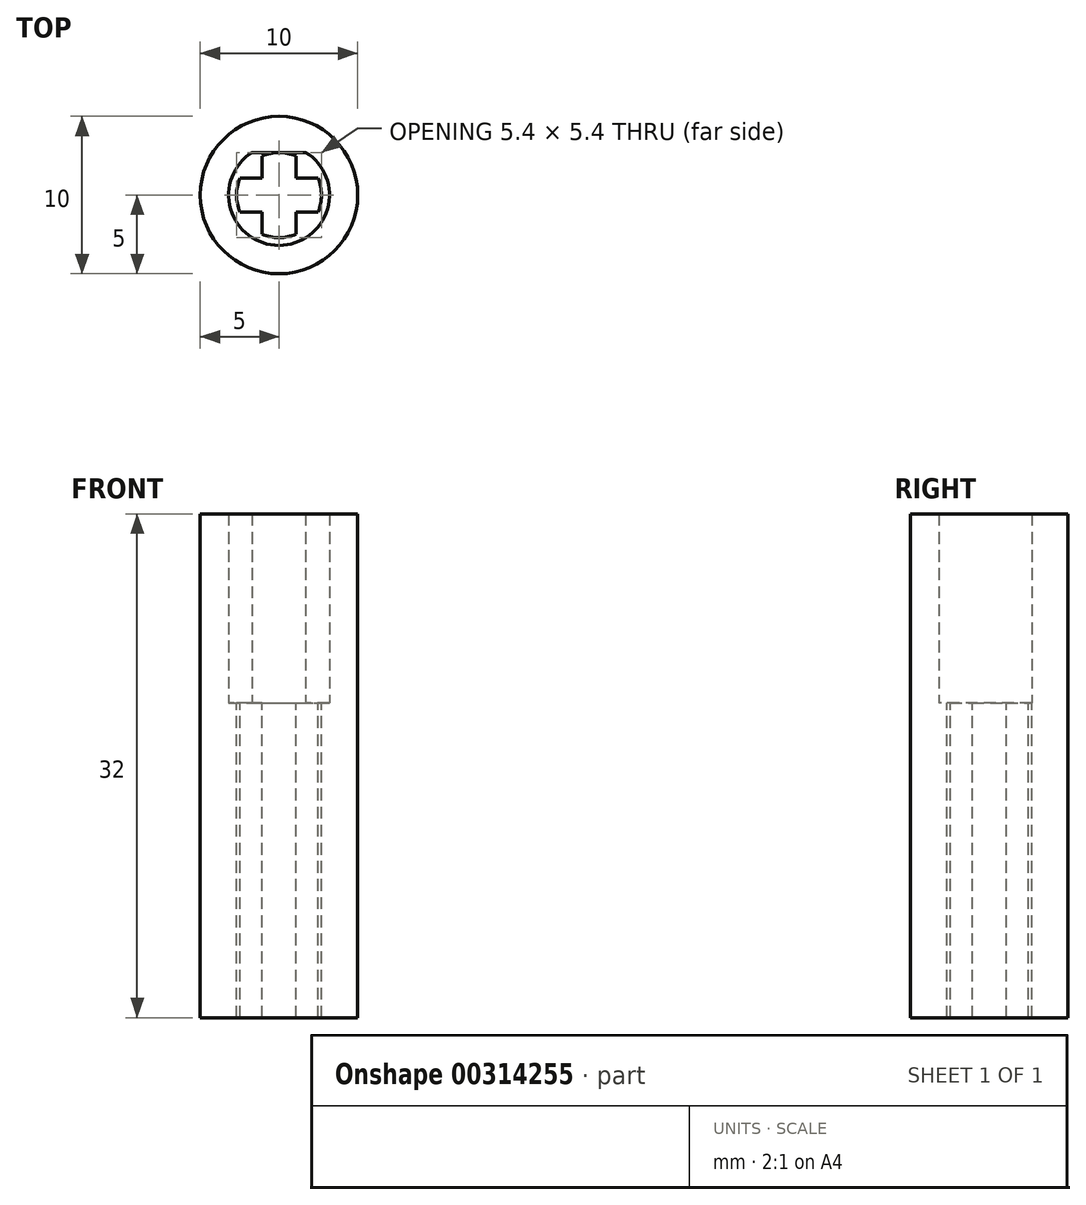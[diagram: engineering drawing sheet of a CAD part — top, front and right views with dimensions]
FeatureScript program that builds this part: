
annotation { "Feature Type Name" : "Feature", "Feature Type Description" : "" }
export const myFeature = defineFeature(function(context is Context, id is Id, definition is map)
    precondition{}
    {
        {
            var Q0;
            Q0=qCreatedBy(makeId("Top.planeOp"),FACE);
            var sketch = newSketch(context, id + "F0", { "sketchPlane" : qUnion([Q0])});
            skCircle(sketch, "E0", {"center": v(0, 0) * mm, "radius": 3.2 * mm});
            skLineSegment(sketch, "E1", {"start": v(-1.7, 2.71) * mm, "end": v(1.7, 2.71) * mm});
            skCircle(sketch, "E2", {"center": v(0, 0) * mm, "radius": 5 * mm});
            skSolve(sketch);
        }
        {
            var Q0;
            Q0=makeQuery(id+"F0.imprint","IMPRINT",FACE,{"disambiguationData":[TD([[makeQuery(id+"F0.imprint","IMPRINT",EDGE,{"derivedFrom":sQuery(id+"F0.wireOp",EDGE,"E2")}),1.0]])]});
            var Q1;
            {var subQ0=sQuery(id+"F0.wireOp",EDGE,"E1");Q1=makeQuery(id+"F0.imprint","IMPRINT",FACE,{"disambiguationData":[TD([[makeQuery(id+"F0.imprint","IMPRINT",EDGE,{"derivedFrom":subQ0}),1.0]])]});}
            extrude(context, id + "F1", {"entities" : qUnion([Q0, Q1]), "depth" : 12 * mm});
        }
        {
            var Q0;
            Q0=qCreatedBy(makeId("Top.planeOp"),FACE);
            var sketch = newSketch(context, id + "F2", { "sketchPlane" : qUnion([Q0])});
            skCircle(sketch, "E3", {"center": v(0, 0) * mm, "radius": 2.7 * mm});
            skLineSegment(sketch, "E4", {"start": v(-1.08, -2.48) * mm, "end": v(-1.08, -1.08) * mm});
            skLineSegment(sketch, "E5", {"start": v(-1.08, -1.08) * mm, "end": v(-2.48, -1.08) * mm});
            skLineSegment(sketch, "E6", {"start": v(-2.48, 1.08) * mm, "end": v(-1.08, 1.08) * mm});
            skLineSegment(sketch, "E7", {"start": v(-1.08, 1.08) * mm, "end": v(-1.08, 2.48) * mm});
            skLineSegment(sketch, "E8", {"start": v(1.08, -2.48) * mm, "end": v(1.08, -1.08) * mm});
            skLineSegment(sketch, "E9", {"start": v(1.08, -1.08) * mm, "end": v(2.48, -1.08) * mm});
            skLineSegment(sketch, "E10", {"start": v(1.08, 2.48) * mm, "end": v(1.08, 1.08) * mm});
            skLineSegment(sketch, "E11", {"start": v(1.08, 1.08) * mm, "end": v(2.48, 1.08) * mm});
            skCircle(sketch, "E12", {"center": v(0, 0) * mm, "radius": 5 * mm});
            skSolve(sketch);
        }
        {
            var Q0;
            Q0=makeQuery(id+"F2.imprint","IMPRINT",FACE,{"disambiguationData":[TD([[makeQuery(id+"F2.imprint","IMPRINT",EDGE,{"derivedFrom":sQuery(id+"F2.wireOp",EDGE,"E12")}),1.0]])]});
            var Q1;
            {var subQ0=sQuery(id+"F2.wireOp",EDGE,"E4");Q1=makeQuery(id+"F2.imprint","IMPRINT",FACE,{"disambiguationData":[TD([[makeQuery(id+"F2.imprint","IMPRINT",EDGE,{"derivedFrom":subQ0}),1.0]])]});}
            var Q2;
            {var subQ0=sQuery(id+"F2.wireOp",EDGE,"E6");Q2=makeQuery(id+"F2.imprint","IMPRINT",FACE,{"disambiguationData":[TD([[makeQuery(id+"F2.imprint","IMPRINT",EDGE,{"derivedFrom":subQ0}),1.0]])]});}
            var Q3;
            {var subQ0=sQuery(id+"F2.wireOp",EDGE,"E10");Q3=makeQuery(id+"F2.imprint","IMPRINT",FACE,{"disambiguationData":[TD([[makeQuery(id+"F2.imprint","IMPRINT",EDGE,{"derivedFrom":subQ0}),1.0]])]});}
            var Q4;
            {var subQ0=sQuery(id+"F2.wireOp",EDGE,"E8");Q4=makeQuery(id+"F2.imprint","IMPRINT",FACE,{"disambiguationData":[TD([[makeQuery(id+"F2.imprint","IMPRINT",EDGE,{"derivedFrom":subQ0}),-1.0]])]});}
            extrude(context, id + "F3", {"entities" : qUnion([Q0, Q1, Q2, Q3, Q4]), "operationType" : NewBodyOperationType.ADD, "depth" : -20 * mm});
        }
    });
